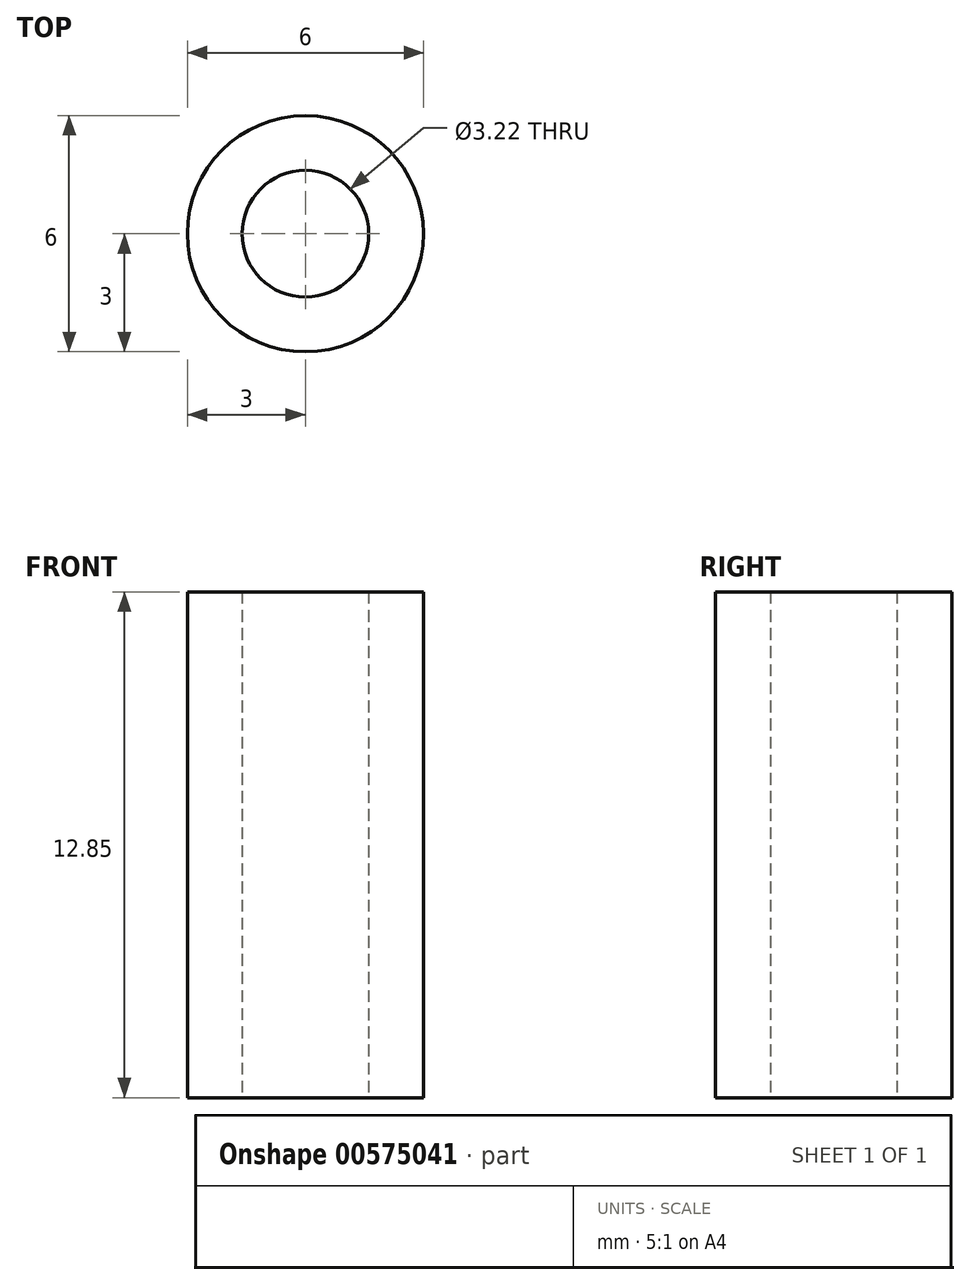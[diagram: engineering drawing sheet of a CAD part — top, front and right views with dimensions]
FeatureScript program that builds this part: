
annotation { "Feature Type Name" : "Feature", "Feature Type Description" : "" }
export const myFeature = defineFeature(function(context is Context, id is Id, definition is map)
    precondition{}
    {
        {
            var Q0;
            Q0=qCreatedBy(makeId("Top.planeOp"),FACE);
            var sketch = newSketch(context, id + "F0", { "sketchPlane" : qUnion([Q0])});
            skCircle(sketch, "E0", {"center": v(0, 0) * mm, "radius": 1.61 * mm});
            skCircle(sketch, "E1", {"center": v(0, 0) * mm, "radius": 3 * mm});
            skSolve(sketch);
        }
        {
            var Q0;
            Q0 = qSketchRegion(id + "F0", true);
            extrude(context, id + "F1", {"entities" : qUnion([Q0]), "depth" : 12.85 * mm, "offsetDistance" : 25 * mm});
        }
    });
